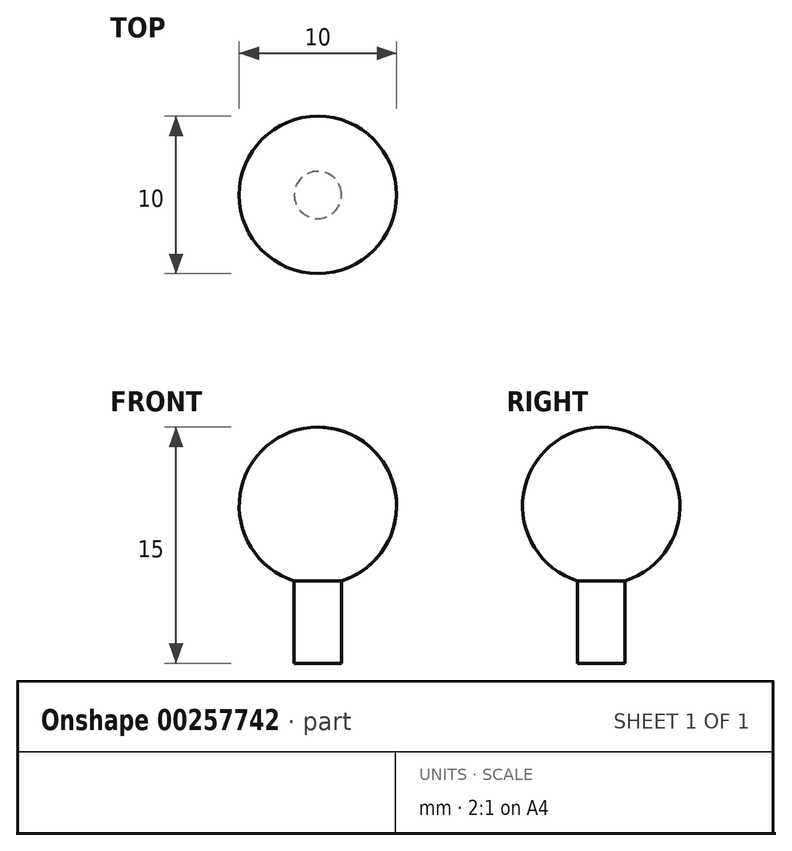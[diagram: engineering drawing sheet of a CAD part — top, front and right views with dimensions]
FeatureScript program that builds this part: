
annotation { "Feature Type Name" : "Feature", "Feature Type Description" : "" }
export const myFeature = defineFeature(function(context is Context, id is Id, definition is map)
    precondition{}
    {
        {
            var Q0;
            Q0=qCreatedBy(makeId("Front.planeOp"),FACE);
            var sketch = newSketch(context, id + "F0", { "sketchPlane" : qUnion([Q0])});
            skArc(sketch, "E0", {"start": v(1.5, -4.77) * mm, "mid": v(4.94, 0.76) * mm, "end": v(0, 5) * mm});
            skLineSegment(sketch, "E1.top", {"start": v(0, -10) * mm, "end": v(1.5, -10) * mm});
            skLineSegment(sketch, "E1.right", {"start": v(1.5, -4.77) * mm, "end": v(1.5, -10) * mm});
            skLineSegment(sketch, "E2", {"start": v(0, 5) * mm, "end": v(0, -10) * mm});
            skSolve(sketch);
        }
        {
            var Q0;
            Q0=makeQuery(id+"F0.imprint","IMPRINT",FACE,{"disambiguationData":[TD([[makeQuery(id+"F0.imprint","IMPRINT",EDGE,{"derivedFrom":sQuery(id+"F0.wireOp",EDGE,"E0")}),1.0]])]});
            var Q1;
            Q1=sQuery(id+"F0.wireOp",EDGE,"E2");
            revolve(context, id + "F1", {"entities" : qUnion([Q0]), "axis" : qUnion([Q1]), "revolveType" : RevolveType.FULL});
        }
    });
